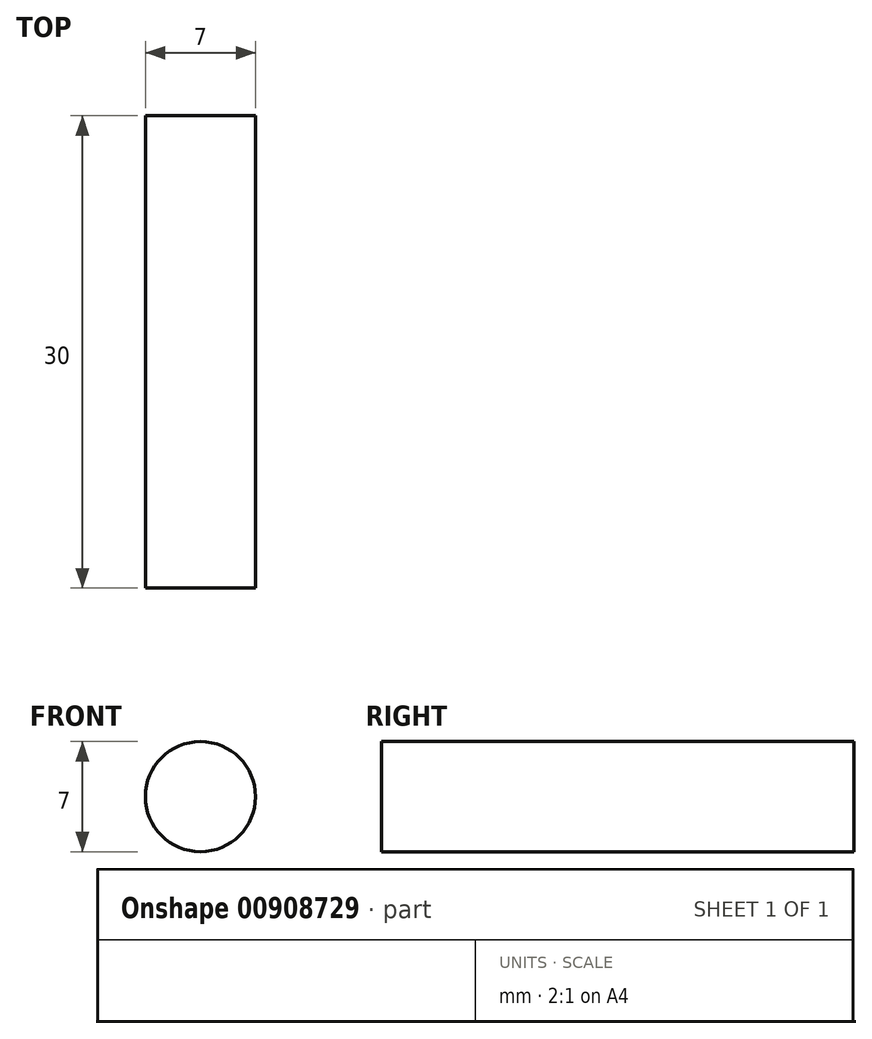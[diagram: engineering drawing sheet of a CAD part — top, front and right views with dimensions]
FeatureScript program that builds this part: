
annotation { "Feature Type Name" : "Feature", "Feature Type Description" : "" }
export const myFeature = defineFeature(function(context is Context, id is Id, definition is map)
    precondition{}
    {
        {
            var Q0;
            Q0=qCreatedBy(makeId("Front.planeOp"),FACE);
            var sketch = newSketch(context, id + "F0", { "sketchPlane" : qUnion([Q0])});
            skCircle(sketch, "E0", {"center": v(0, 0) * mm, "radius": 3.5 * mm});
            skSolve(sketch);
        }
        {
            var Q0;
            Q0=makeQuery(id+"F0.imprint","IMPRINT",FACE,{"disambiguationData":[TD([[makeQuery(id+"F0.imprint","IMPRINT",EDGE,{"derivedFrom":sQuery(id+"F0.wireOp",EDGE,"E0")}),1.0]])]});
            extrude(context, id + "F1", {"entities" : qUnion([Q0]), "depth" : 30 * mm, "offsetDistance" : 25 * mm, "symmetric" : true});
        }
    });
